# Revit family: Quincy
name_source: partatom
category: Furniture
revit_build: Autodesk Revit 2016 (Build: 20151209_0715(x64)
units: mm (PartAtom-declared; Revit-internal decimal feet)

## family parameters
Always vertical = Yes
Cut with Voids When Loaded = No
OmniClass Number = 23.40.20.00
OmniClass Title = General Furniture and Specialties
Room Calculation Point = No
Shared = No
Work Plane-Based = No

## types (5) — shared parameters
Depth = 34"
Seat Height = 20"

## per-type parameters (varying)
| type | Base | Cushion 2 | Cushion 3 | Cushion Width | Furniture Geometry | Ottoman Feet | Seat Depth | Seat Width | Slide Out Ottoman |
| Chair | Yes | No | No | 19 1/2" | Yes | No | 22" | 19 1/2" | No |
| Sofa | Yes | Yes | Yes | 19 1/2" | Yes | No | 22" | 58 1/2" | No |
| Loveseat | Yes | Yes | No | 19 1/2" | Yes | No | 22" | 39" | No |
| Chair-Slide Out Ottoman | No | No | No | 19 1/2" | Yes | No | 22" | 19 1/2" | Yes |
| Ottoman | Yes | No | No | 28 1/2" | No | Yes | 22 1/2" | 28 1/2" | No |

## geometry (parser evidence)
native form markers: Blend x8, Sweep x45
no freeform markers — native parametric forms only
